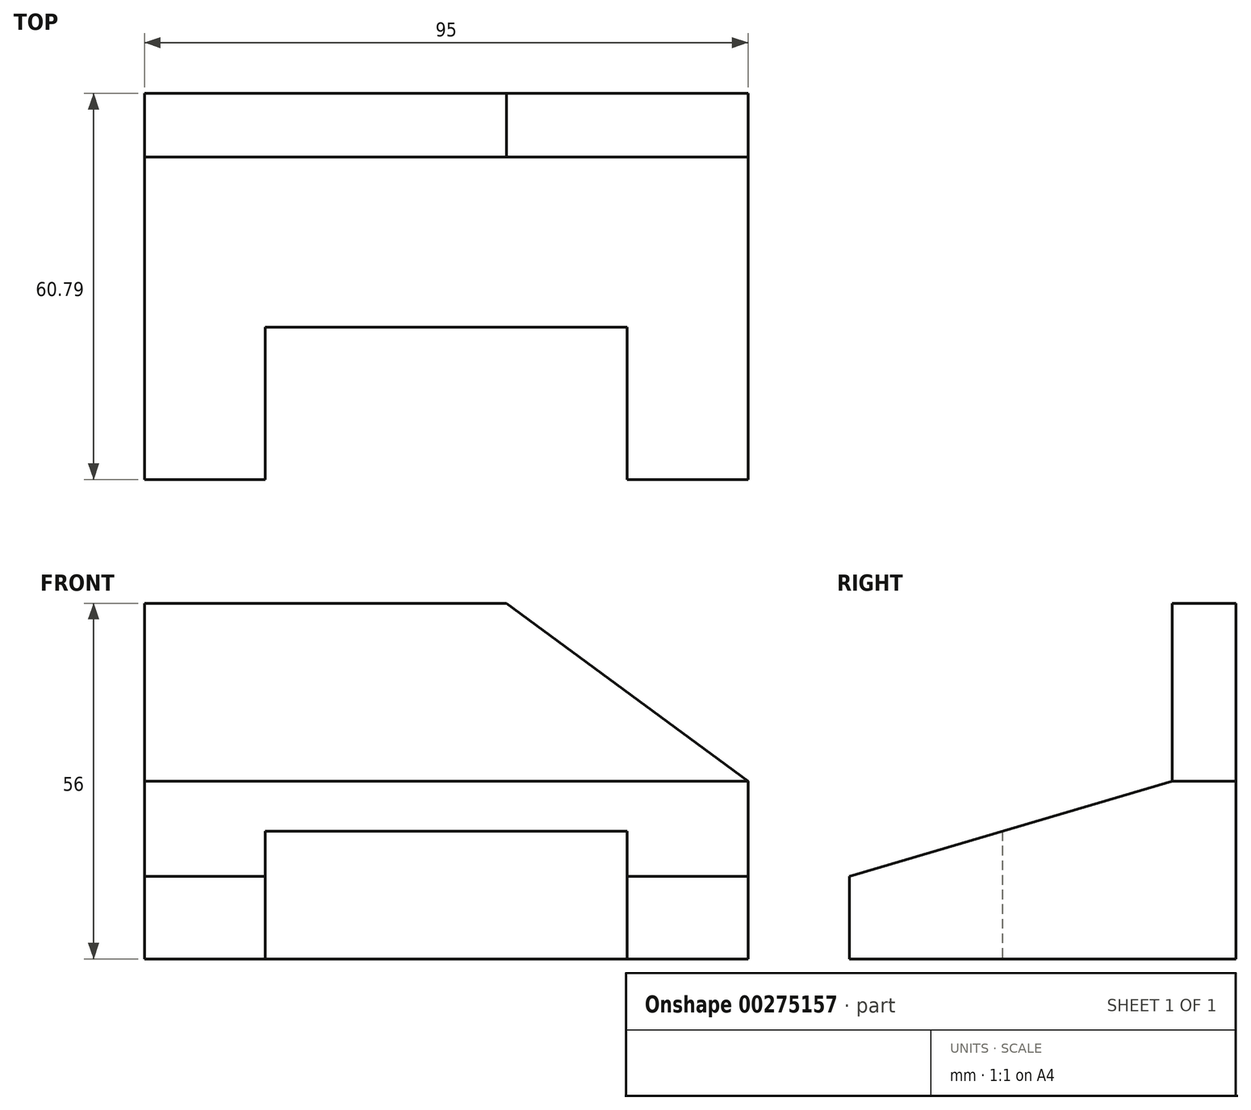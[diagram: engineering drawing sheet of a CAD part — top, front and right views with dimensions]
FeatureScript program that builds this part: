
annotation { "Feature Type Name" : "Feature", "Feature Type Description" : "" }
export const myFeature = defineFeature(function(context is Context, id is Id, definition is map)
    precondition{}
    {
        {
            var Q0;
            Q0=qCreatedBy(makeId("Right.planeOp"),FACE);
            var sketch = newSketch(context, id + "F0", { "sketchPlane" : qUnion([Q0])});
            skLineSegment(sketch, "E0.bottom", {"start": v(-10, 56) * mm, "end": v(0, 56) * mm});
            skLineSegment(sketch, "E0.left", {"start": v(-10, 56) * mm, "end": v(-10, 28) * mm});
            skLineSegment(sketch, "E0.right", {"start": v(0, 56) * mm, "end": v(0, 28) * mm});
            skLineSegment(sketch, "E1", {"start": v(-60.8, 0) * mm, "end": v(-60.8, 13) * mm});
            skLineSegment(sketch, "E2", {"start": v(-60.8, 13) * mm, "end": v(-10, 28) * mm});
            skLineSegment(sketch, "E3", {"start": v(0, 28) * mm, "end": v(0, 0) * mm});
            skLineSegment(sketch, "E4", {"start": v(-60.8, 0) * mm, "end": v(-10, 0) * mm});
            skLineSegment(sketch, "E5", {"start": v(-10, 0) * mm, "end": v(0, 0) * mm});
            skSolve(sketch);
        }
        {
            var Q0;
            Q0 = qSketchRegion(id + "F0", true);
            extrude(context, id + "F1", {"entities" : qUnion([Q0]), "depth" : 95 * mm});
        }
        {
            var Q0;
            Q0=makeQuery(id+"F1.opExtrude","SWEPT_FACE",FACE,{"disambiguationData":[OSD([sQuery(id+"F0.wireOp",EDGE,"E0.left")])]});
            var sketch = newSketch(context, id + "F2", { "sketchPlane" : qUnion([Q0])});
            skLineSegment(sketch, "E6", {"start": v(57, 56) * mm, "end": v(95, 28) * mm});
            skSolve(sketch);
        }
        {
            var Q0;
            {var subQ0=sQuery(id+"F2.wireOp",EDGE,"E6");Q0=makeQuery(id+"F2.imprint","IMPRINT",FACE,{"disambiguationData":[TD([[makeQuery(id+"F2.imprint","IMPRINT",EDGE,{"derivedFrom":subQ0}),1.0]])]});}
            extrude(context, id + "F3", {"entities" : qUnion([Q0]), "operationType" : NewBodyOperationType.REMOVE, "endBound" : BoundingType.UP_TO_NEXT, "oppositeDirection" : true, "depth" : 25 * mm});
        }
        {
            var Q0;
            Q0=makeQuery(id+"F1.opExtrude","SWEPT_FACE",FACE,{"disambiguationData":[OSD([sQuery(id+"F0.wireOp",EDGE,"E4"),sQuery(id+"F0.wireOp",EDGE,"E5")])]});
            var sketch = newSketch(context, id + "F4", { "sketchPlane" : qUnion([Q0])});
            skLineSegment(sketch, "E7.bottom", {"start": v(19, 60.8) * mm, "end": v(76, 60.8) * mm});
            skLineSegment(sketch, "E7.top", {"start": v(19, 36.8) * mm, "end": v(76, 36.8) * mm});
            skLineSegment(sketch, "E7.left", {"start": v(19, 60.8) * mm, "end": v(19, 36.8) * mm});
            skLineSegment(sketch, "E7.right", {"start": v(76, 60.8) * mm, "end": v(76, 36.8) * mm});
            skSolve(sketch);
        }
        {
            var Q0;
            Q0=makeQuery(id+"F4.imprint","IMPRINT",FACE,{"disambiguationData":[TD([[makeQuery(id+"F4.imprint","IMPRINT",EDGE,{"derivedFrom":sQuery(id+"F4.wireOp",EDGE,"E7.bottom")}),1.0]])]});
            extrude(context, id + "F5", {"entities" : qUnion([Q0]), "operationType" : NewBodyOperationType.REMOVE, "oppositeDirection" : true, "depth" : 55.8 * mm});
        }
    });
